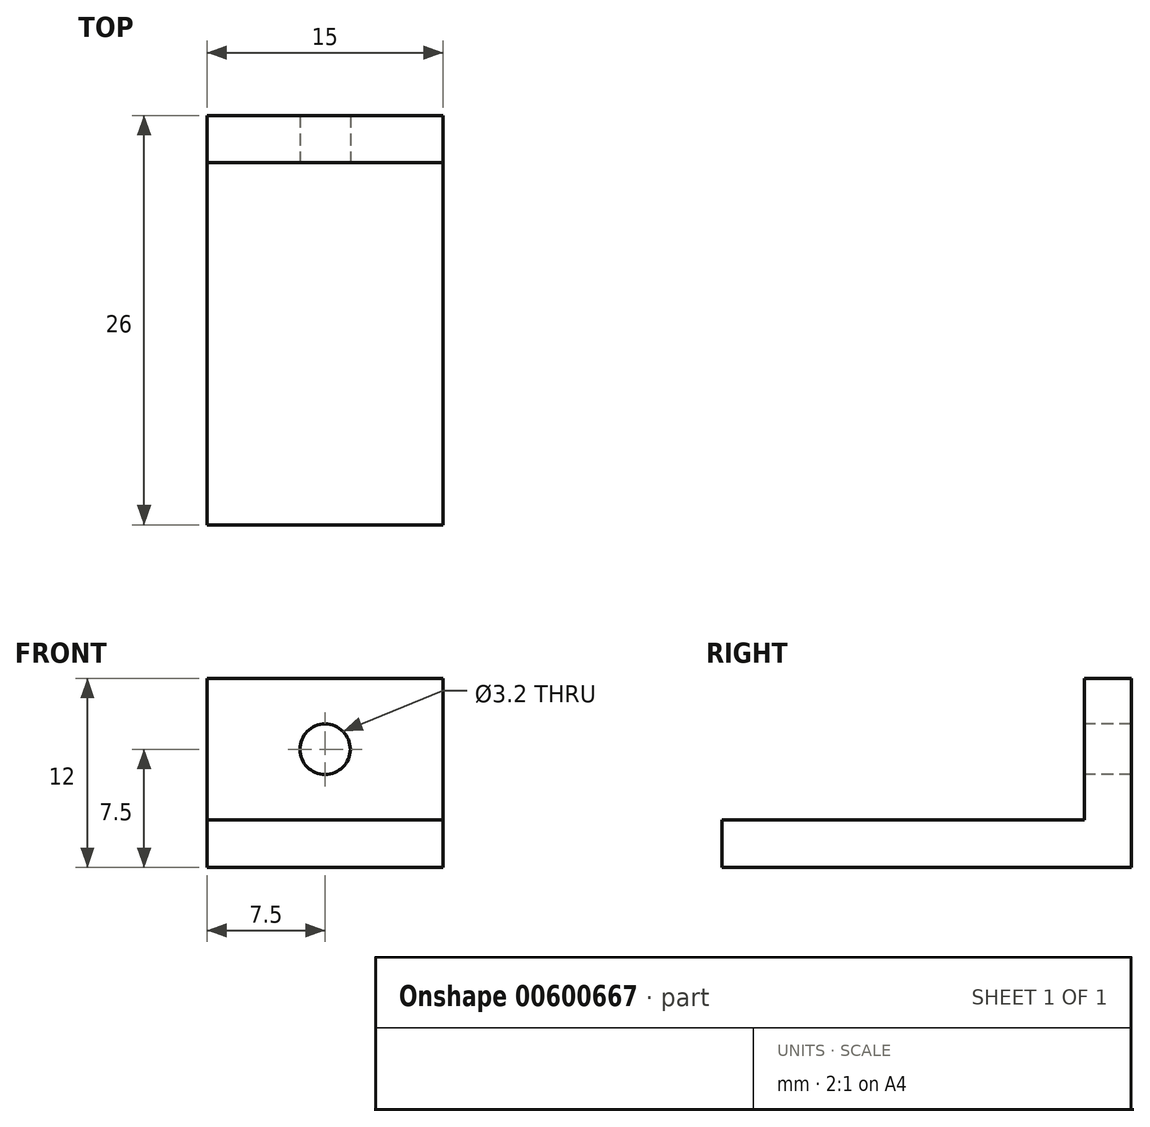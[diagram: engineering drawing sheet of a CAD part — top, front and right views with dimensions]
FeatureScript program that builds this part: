
annotation { "Feature Type Name" : "Feature", "Feature Type Description" : "" }
export const myFeature = defineFeature(function(context is Context, id is Id, definition is map)
    precondition{}
    {
        {
            var Q0;
            Q0=qCreatedBy(makeId("Top.planeOp"),FACE);
            var sketch = newSketch(context, id + "F0", { "sketchPlane" : qUnion([Q0])});
            skLineSegment(sketch, "E0.bottom", {"start": v(0, 0) * mm, "end": v(15, 0) * mm});
            skLineSegment(sketch, "E0.top", {"start": v(0, 26) * mm, "end": v(15, 26) * mm});
            skLineSegment(sketch, "E0.left", {"start": v(0, 0) * mm, "end": v(0, 26) * mm});
            skLineSegment(sketch, "E0.right", {"start": v(15, 0) * mm, "end": v(15, 26) * mm});
            skLineSegment(sketch, "E1.top", {"start": v(0, 23) * mm, "end": v(15, 23) * mm});
            skLineSegment(sketch, "E1.left", {"start": v(0, 26) * mm, "end": v(0, 23) * mm});
            skLineSegment(sketch, "E1.right", {"start": v(15, 26) * mm, "end": v(15, 23) * mm});
            skSolve(sketch);
        }
        {
            var Q0;
            Q0=makeQuery(id+"F0.imprint","IMPRINT",FACE,{"disambiguationData":[TD([[makeQuery(id+"F0.imprint","IMPRINT",EDGE,{"derivedFrom":sQuery(id+"F0.wireOp",EDGE,"E0.bottom")}),1.0]])]});
            extrude(context, id + "F1", {"entities" : qUnion([Q0]), "depth" : 3 * mm, "offsetDistance" : 25 * mm});
        }
        {
            var Q0;
            Q0=makeQuery(id+"F0.imprint","IMPRINT",FACE,{"disambiguationData":[TD([[makeQuery(id+"F0.imprint","IMPRINT",EDGE,{"derivedFrom":sQuery(id+"F0.wireOp",EDGE,"E0.top")}),-1.0]])]});
            extrude(context, id + "F2", {"entities" : qUnion([Q0]), "operationType" : NewBodyOperationType.ADD, "depth" : 12 * mm, "offsetDistance" : 25 * mm});
        }
        {
            var Q0;
            Q0=makeQuery(id+"F2.opExtrude","SWEPT_FACE",FACE,{"disambiguationData":[OSD([sQuery(id+"F0.wireOp",EDGE,"E1.top")])]});
            var sketch = newSketch(context, id + "F3", { "sketchPlane" : qUnion([Q0])});
            skLineSegment(sketch, "E2", {"start": v(7.5, 12) * mm, "end": v(7.5, 3) * mm});
            skPoint(sketch, "E3", {"position": v(7.5, 7.5) * mm});
            skSolve(sketch);
        }
        {
            var Q0;
            Q0=sQuery(id+"F3.wireOp",VERTEX,"E3");
            var Q1;
            Q1=makeQuery(id+"F1.opExtrude","SWEPT_BODY",BODY,{"disambiguationData":[OSD([sQuery(id+"F0.wireOp",EDGE,"E0.bottom"),sQuery(id+"F0.wireOp",EDGE,"E0.left"),sQuery(id+"F0.wireOp",EDGE,"E0.right"),sQuery(id+"F0.wireOp",EDGE,"E1.top")])]});
            hole(context, id + "F4", {"style" : HoleStyle.SIMPLE, "endStyle" : HoleEndStyle.THROUGH, "holeDiameter" : 3.2 * mm, "majorDiameter" : 5 * mm, "isTappedThrough" : true, "tappedDepth" : 12 * mm, "tapClearance" : 3, "locations" : qUnion([Q0]), "scope" : qUnion([Q1])});
        }
    });
